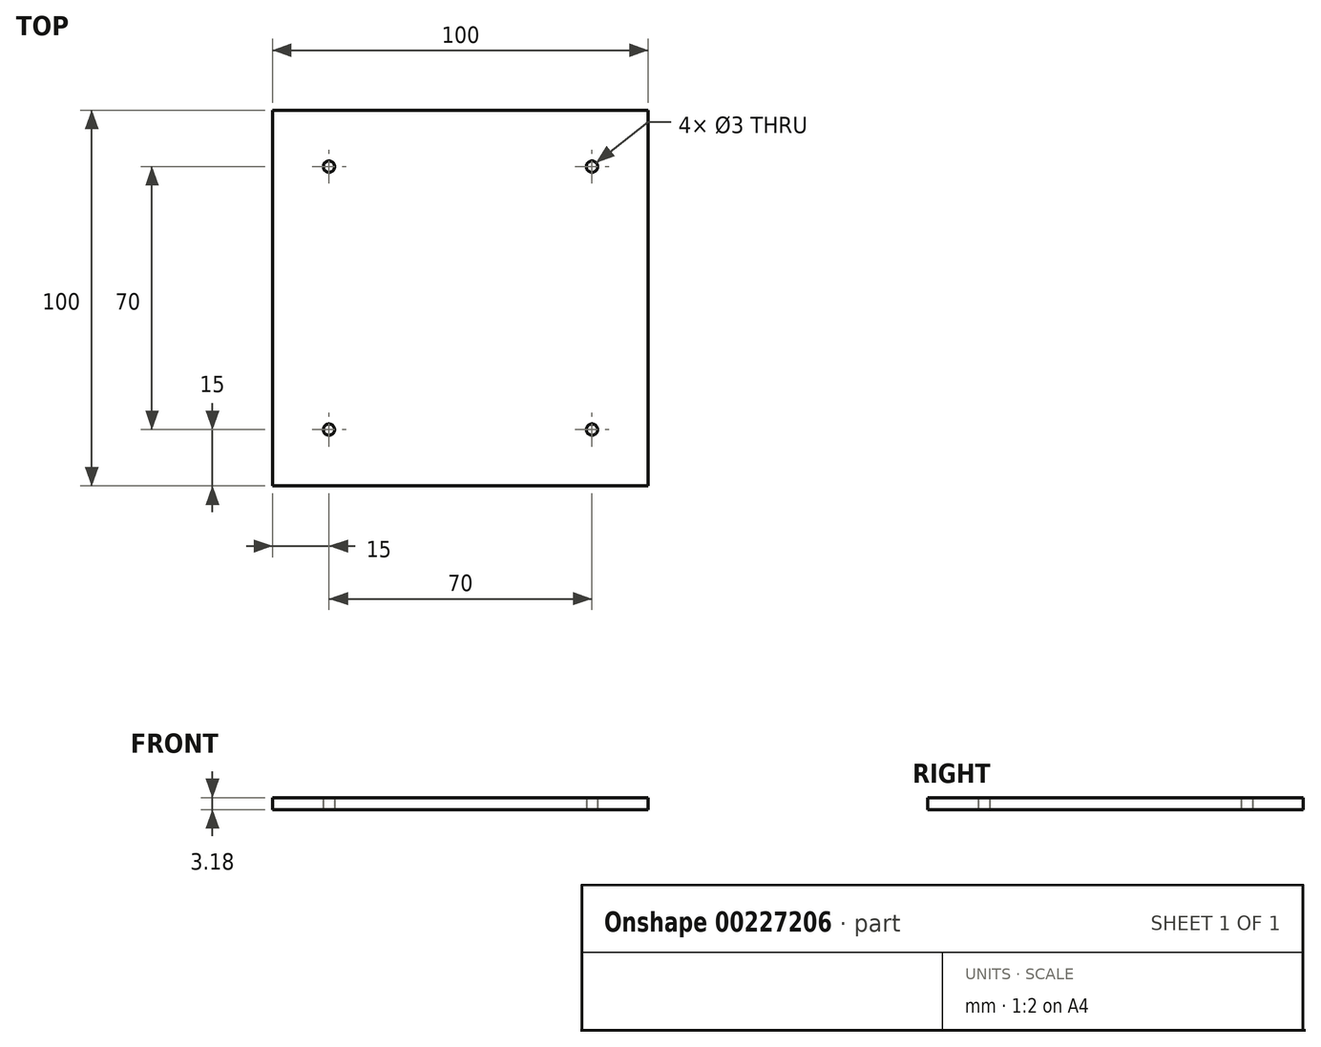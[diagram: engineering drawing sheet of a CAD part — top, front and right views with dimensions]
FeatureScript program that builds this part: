
annotation { "Feature Type Name" : "Feature", "Feature Type Description" : "" }
export const myFeature = defineFeature(function(context is Context, id is Id, definition is map)
    precondition{}
    {
        {
            var Q0;
            Q0=qCreatedBy(makeId("Top.planeOp"),FACE);
            var sketch = newSketch(context, id + "F0", { "sketchPlane" : qUnion([Q0])});
            skLineSegment(sketch, "E0.bottom", {"start": v(50, -50) * mm, "end": v(-50, -50) * mm});
            skLineSegment(sketch, "E0.top", {"start": v(50, 50) * mm, "end": v(-50, 50) * mm});
            skLineSegment(sketch, "E0.left", {"start": v(50, -50) * mm, "end": v(50, 50) * mm});
            skLineSegment(sketch, "E0.right", {"start": v(-50, -50) * mm, "end": v(-50, 50) * mm});
            skPoint(sketch, "E0.middle", {"position": v(0, 0) * mm});
            skCircle(sketch, "E1", {"center": v(-35, 35) * mm, "radius": 1.5 * mm});
            skCircle(sketch, "E2.1.0", {"center": v(-35, -35) * mm, "radius": 1.5 * mm});
            skCircle(sketch, "E2.2.0", {"center": v(35, -35) * mm, "radius": 1.5 * mm});
            skCircle(sketch, "E2.3.0", {"center": v(35, 35) * mm, "radius": 1.5 * mm});
            skSolve(sketch);
        }
        {
            var Q0;
            Q0 = qSketchRegion(id + "F0", true);
            extrude(context, id + "F1", {"entities" : qUnion([Q0]), "depth" : 3.17 * mm});
        }
    });
